# Revit family: NAU_Naughtone_Tbls_Hue
name_source: partatom
category: Furniture
revit_build: Autodesk Revit 2018 (Build: 20170223_1515(x64)
units: mm (PartAtom-declared; Revit-internal decimal feet)

## family parameters
Always vertical = Yes
Cut with Voids When Loaded = No
OmniClass Number = 23.40.20.00
OmniClass Title = General Furniture and Specialties
Room Calculation Point = No
Shared = Yes
Work Plane-Based = No

## types (2) — shared parameters
Assembly Code = E2020200
AssetType = Movable
BIMObjectName = NAU_Naughtone_Tables_Hue
Category = Pr_40_50_21 : Desks, tables and worktops
Color = Various
DurationUnit = year
Finish = White or Black MFMDF top; or Oak or Walnut veneer top. Polised MDF edge detail.
IfcExportAs = IfcFurnishingElementType
IfcExportType = TABLE
Keynote = Pr_40_50_21
MainColor = Various
ManufacturerAddress = Knaresborough Tech Park, Manse Lane, Knaresborough, HG5 8LF
ManufacturerName = Naughtone
ManufacturerURL = www.naughtone.com
Material = Base in 16 RAL Colours
NBSDescription = Tables
NBSReference = 45-35-86/327
Name = Tables_Hue_Naughtone
NominalLength = 1300 mm  [stored 4.26509 ft]
NominalWidth = 700 mm  [stored 2.29659 ft]
ProductInformation = www.naughtone.com/products/hue-2/
Revision = 0
Shape = Rectangular
SustainabilityPerformance = FSC certified. FISP certified. ISO 14001
URL = www.naughtone.com
Uniclass2015Code = Pr_40_50_21
Uniclass2015Title = Desks, tables and worktops
Version = 1
WarrantyDescription = Request warranty information from naughtone
WarrantyDurationLabor = 7
WarrantyDurationParts = 7
WarrantyDurationUnit = year
zero-valued in all types: NumberOfChairs, WorksurfaceArea

## per-type parameters (varying)
| type | Description | Model | ModelNumber | ModelReference | NominalHeight | Size |
| HUET130X70 - Hue Rectangular Table | Hue Rectangular Table | HUET130X70 | HUET130X70 | Hue Rectangular Table | 750 mm  [stored 2.46063 ft] | 700 x 1300 x 750mm |
| HUEBHT130X70 - Hue Rectangular Bar Height Table | Hue Rectangular Bar Height Table | HUEBHT130X70 | HUEBHT130X70 | Hue Rectangular Bar Height Table | 1000 mm  [stored 3.28084 ft] | 700 x 1300 x 1000mm |

note: [stored X ft] marks values corroborated as IEEE doubles in the binary element streams (Revit-internal decimal feet)

## geometry (parser evidence)
native form markers: Sweep x2
no freeform markers — native parametric forms only
